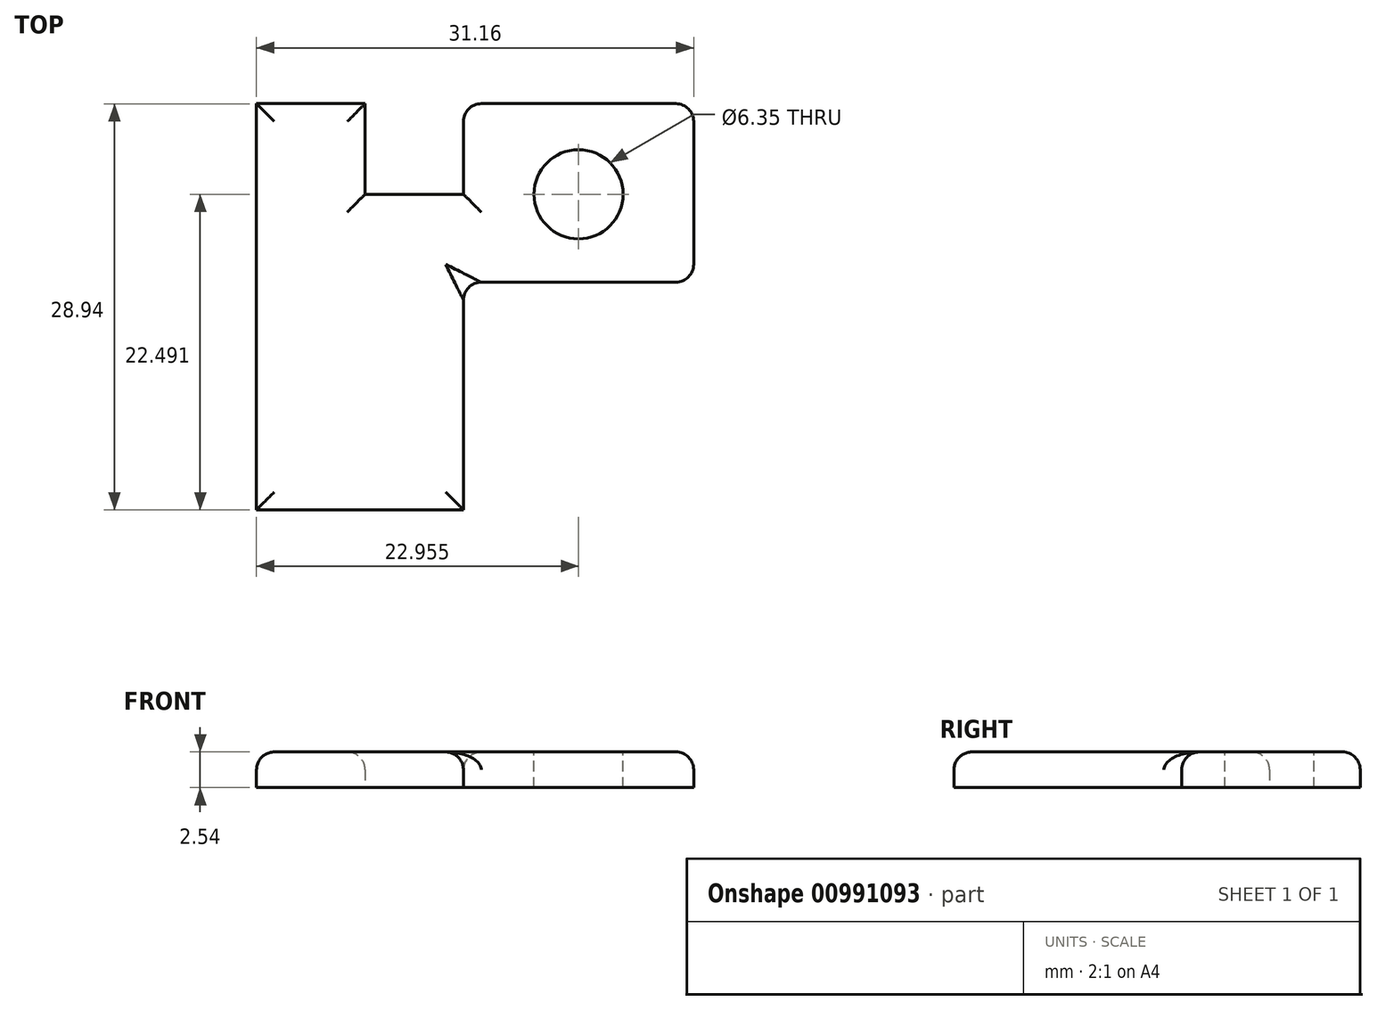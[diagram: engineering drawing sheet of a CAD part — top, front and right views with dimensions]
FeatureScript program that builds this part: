
annotation { "Feature Type Name" : "Feature", "Feature Type Description" : "" }
export const myFeature = defineFeature(function(context is Context, id is Id, definition is map)
    precondition{}
    {
        {
            var Q0;
            Q0=qCreatedBy(makeId("Top.planeOp"),FACE);
            var sketch = newSketch(context, id + "F0", { "sketchPlane" : qUnion([Q0])});
            skLineSegment(sketch, "E0.bottom", {"start": v(-44.34, 38.25) * mm, "end": v(-13.18, 38.25) * mm});
            skLineSegment(sketch, "E0.top", {"start": v(-44.34, 9.3) * mm, "end": v(-13.18, 9.3) * mm});
            skLineSegment(sketch, "E0.left", {"start": v(-44.34, 38.25) * mm, "end": v(-44.34, 9.3) * mm});
            skLineSegment(sketch, "E0.right", {"start": v(-13.18, 38.25) * mm, "end": v(-13.18, 9.3) * mm});
            skLineSegment(sketch, "E1.bottom", {"start": v(-13.18, 9.3) * mm, "end": v(-29.59, 9.3) * mm});
            skLineSegment(sketch, "E1.top", {"start": v(-13.18, 25.53) * mm, "end": v(-29.59, 25.53) * mm});
            skLineSegment(sketch, "E1.left", {"start": v(-13.18, 9.3) * mm, "end": v(-13.18, 25.53) * mm});
            skLineSegment(sketch, "E1.right", {"start": v(-29.59, 9.3) * mm, "end": v(-29.59, 25.53) * mm});
            skLineSegment(sketch, "E2.bottom", {"start": v(-29.59, 38.25) * mm, "end": v(-36.6, 38.25) * mm});
            skLineSegment(sketch, "E2.top", {"start": v(-29.59, 31.8) * mm, "end": v(-36.6, 31.8) * mm});
            skLineSegment(sketch, "E2.left", {"start": v(-29.59, 38.25) * mm, "end": v(-29.59, 31.8) * mm});
            skLineSegment(sketch, "E2.right", {"start": v(-36.6, 38.25) * mm, "end": v(-36.6, 31.8) * mm});
            skSolve(sketch);
        }
        {
            var Q0;
            {var subQ2=sQuery(id+"F0.wireOp",EDGE,"E0.left");Q0=makeQuery(id+"F0.imprint","IMPRINT",FACE,{"disambiguationData":[TD([[makeQuery(id+"F0.imprint","IMPRINT",EDGE,{"derivedFrom":subQ2}),1.0]])]});}
            extrude(context, id + "F1", {"entities" : qUnion([Q0]), "depth" : 2.54 * mm, "offsetDistance" : 25.4 * mm});
        }
        {
            var Q0;
            Q0=makeQuery(id+"F1.opExtrude","CAP_FACE",FACE,{"disambiguationData":[OSD([sQuery(id+"F0.wireOp",EDGE,"E0.bottom"),sQuery(id+"F0.wireOp",EDGE,"E0.top"),sQuery(id+"F0.wireOp",EDGE,"E0.left"),sQuery(id+"F0.wireOp",EDGE,"E0.right"),sQuery(id+"F0.wireOp",EDGE,"E1.top"),sQuery(id+"F0.wireOp",EDGE,"E1.right"),sQuery(id+"F0.wireOp",EDGE,"E2.top"),sQuery(id+"F0.wireOp",EDGE,"E2.left"),sQuery(id+"F0.wireOp",EDGE,"E2.right")])],"isStart":false});
            var sketch = newSketch(context, id + "F2", { "sketchPlane" : qUnion([Q0])});
            skPoint(sketch, "E3", {"position": v(-21.39, 38.25) * mm});
            skPoint(sketch, "E4", {"position": v(-21.39, 25.53) * mm});
            skPoint(sketch, "E5", {"position": v(-21.39, 31.8) * mm});
            skSolve(sketch);
        }
        {
            var Q0;
            Q0=sQuery(id+"F2.wireOp",VERTEX,"E5");
            var Q1;
            Q1=makeQuery(id+"F1.opExtrude","SWEPT_BODY",BODY,{"disambiguationData":[OSD([sQuery(id+"F0.wireOp",EDGE,"E0.bottom"),sQuery(id+"F0.wireOp",EDGE,"E0.top"),sQuery(id+"F0.wireOp",EDGE,"E0.left"),sQuery(id+"F0.wireOp",EDGE,"E0.right"),sQuery(id+"F0.wireOp",EDGE,"E1.top"),sQuery(id+"F0.wireOp",EDGE,"E1.right"),sQuery(id+"F0.wireOp",EDGE,"E2.top"),sQuery(id+"F0.wireOp",EDGE,"E2.left"),sQuery(id+"F0.wireOp",EDGE,"E2.right")])]});
            hole(context, id + "F3", {"style" : HoleStyle.SIMPLE, "endStyle" : HoleEndStyle.THROUGH, "holeDiameter" : 6.35 * mm, "majorDiameter" : 6.35 * mm, "isTappedThrough" : true, "tappedDepth" : 12.7 * mm, "tapClearance" : 3, "locations" : qUnion([Q0]), "scope" : qUnion([Q1])});
        }
        {
            var Q0;
            Q0=makeQuery(id+"F1.opExtrude","CAP_EDGE",EDGE,{"disambiguationData":[OSD([sQuery(id+"F0.wireOp",EDGE,"E0.left")])],"isStart":false});
            var Q1;
            Q1=makeQuery(id+"F1.opExtrude","CAP_EDGE",EDGE,{"disambiguationData":[OSD([sQuery(id+"F0.wireOp",EDGE,"E0.right")])],"isStart":false});
            var Q2;
            Q2=makeQuery(id+"F1.opExtrude","CAP_EDGE",EDGE,{"disambiguationData":[OSD([sQuery(id+"F0.wireOp",EDGE,"E1.top")])],"isStart":false});
            var Q3;
            {var subQ0=sQuery(id+"F0.wireOp",EDGE,"E0.bottom");Q3=makeQuery(id+"F1.opExtrude","CAP_EDGE",EDGE,{"disambiguationData":[OSD([subQ0]),TDD([makeQuery(id+"F0.imprint","IMPRINT",EDGE,{"disambiguationData":[TD([[makeQuery(id+"F0.imprint","INTERSECT",VERTEX,{"derivedFrom":[subQ0,sQuery(id+"F0.wireOp",EDGE,"E2.left")]}),-1.0]])],"derivedFrom":subQ0})])],"isStart":false});}
            var Q4;
            Q4=makeQuery(id+"F1.opExtrude","CAP_EDGE",EDGE,{"disambiguationData":[OSD([sQuery(id+"F0.wireOp",EDGE,"E2.left")])],"isStart":false});
            var Q5;
            Q5=makeQuery(id+"F1.opExtrude","CAP_EDGE",EDGE,{"disambiguationData":[OSD([sQuery(id+"F0.wireOp",EDGE,"E2.top")])],"isStart":false});
            var Q6;
            Q6=makeQuery(id+"F1.opExtrude","CAP_EDGE",EDGE,{"disambiguationData":[OSD([sQuery(id+"F0.wireOp",EDGE,"E2.right")])],"isStart":false});
            var Q7;
            {var subQ0=sQuery(id+"F0.wireOp",EDGE,"E0.bottom");Q7=makeQuery(id+"F1.opExtrude","CAP_EDGE",EDGE,{"disambiguationData":[OSD([subQ0]),TDD([makeQuery(id+"F0.imprint","IMPRINT",EDGE,{"disambiguationData":[TD([[makeQuery(id+"F0.imprint","INTERSECT",VERTEX,{"derivedFrom":[subQ0,sQuery(id+"F0.wireOp",EDGE,"E0.left")]}),-1.0]])],"derivedFrom":subQ0})])],"isStart":false});}
            var Q8;
            Q8=makeQuery(id+"F1.opExtrude","CAP_EDGE",EDGE,{"disambiguationData":[OSD([sQuery(id+"F0.wireOp",EDGE,"E0.top")])],"isStart":false});
            var Q9;
            Q9=makeQuery(id+"F1.opExtrude","CAP_EDGE",EDGE,{"disambiguationData":[OSD([sQuery(id+"F0.wireOp",EDGE,"E1.right")])],"isStart":false});
            fillet(context, id + "F4", {"entities" : qUnion([Q0, Q1, Q2, Q3, Q4, Q5, Q6, Q7, Q8, Q9]), "radius" : 1.27 * mm, "tangentPropagation" : true, "allowEdgeOverflow" : false});
        }
        {
            var Q0;
            Q0=makeQuery(id+"F4.opFillet","BLEND_EDGE",EDGE,{"blendedFrom":[makeQuery(id+"F1.opExtrude","CAP_EDGE",EDGE,{"disambiguationData":[OSD([sQuery(id+"F0.wireOp",EDGE,"E0.right")])],"isStart":false}),makeQuery(id+"F1.opExtrude","CAP_EDGE",EDGE,{"disambiguationData":[OSD([sQuery(id+"F0.wireOp",EDGE,"E1.top")])],"isStart":false})],"blendedInto":[]});
            fillet(context, id + "F5", {"entities" : qUnion([Q0]), "radius" : 1.27 * mm, "tangentPropagation" : true, "allowEdgeOverflow" : false});
        }
        {
            var Q0;
            {var subQ0=sQuery(id+"F0.wireOp",EDGE,"E0.right");var subQ1=sQuery(id+"F0.wireOp",EDGE,"E0.bottom");Q0=makeQuery(id+"F4.opFillet","BLEND_EDGE",EDGE,{"blendedFrom":[makeQuery(id+"F1.opExtrude","CAP_EDGE",EDGE,{"disambiguationData":[OSD([subQ1]),TDD([makeQuery(id+"F0.imprint","IMPRINT",EDGE,{"disambiguationData":[TD([[makeQuery(id+"F0.imprint","INTERSECT",VERTEX,{"derivedFrom":[subQ1,sQuery(id+"F0.wireOp",EDGE,"E2.left")]}),-1.0]])],"derivedFrom":subQ1})])],"isStart":false}),makeQuery(id+"F1.opExtrude","CAP_EDGE",EDGE,{"disambiguationData":[OSD([subQ0])],"isStart":false})],"blendedInto":[]});}
            var Q1;
            {var subQ0=sQuery(id+"F0.wireOp",EDGE,"E2.left");var subQ1=sQuery(id+"F0.wireOp",EDGE,"E0.bottom");Q1=makeQuery(id+"F4.opFillet","BLEND_EDGE",EDGE,{"blendedFrom":[makeQuery(id+"F1.opExtrude","CAP_EDGE",EDGE,{"disambiguationData":[OSD([subQ1]),TDD([makeQuery(id+"F0.imprint","IMPRINT",EDGE,{"disambiguationData":[TD([[makeQuery(id+"F0.imprint","INTERSECT",VERTEX,{"derivedFrom":[subQ1,subQ0]}),-1.0]])],"derivedFrom":subQ1})])],"isStart":false}),makeQuery(id+"F1.opExtrude","CAP_EDGE",EDGE,{"disambiguationData":[OSD([subQ0])],"isStart":false})],"blendedInto":[]});}
            var Q2;
            Q2=makeQuery(id+"F4.opFillet","BLEND_EDGE",EDGE,{"blendedFrom":[makeQuery(id+"F1.opExtrude","CAP_EDGE",EDGE,{"disambiguationData":[OSD([sQuery(id+"F0.wireOp",EDGE,"E1.top")])],"isStart":false}),makeQuery(id+"F1.opExtrude","CAP_EDGE",EDGE,{"disambiguationData":[OSD([sQuery(id+"F0.wireOp",EDGE,"E1.right")])],"isStart":false})],"blendedInto":[]});
            fillet(context, id + "F6", {"entities" : qUnion([Q0, Q1, Q2]), "radius" : 1.27 * mm, "tangentPropagation" : true, "allowEdgeOverflow" : false});
        }
    });
